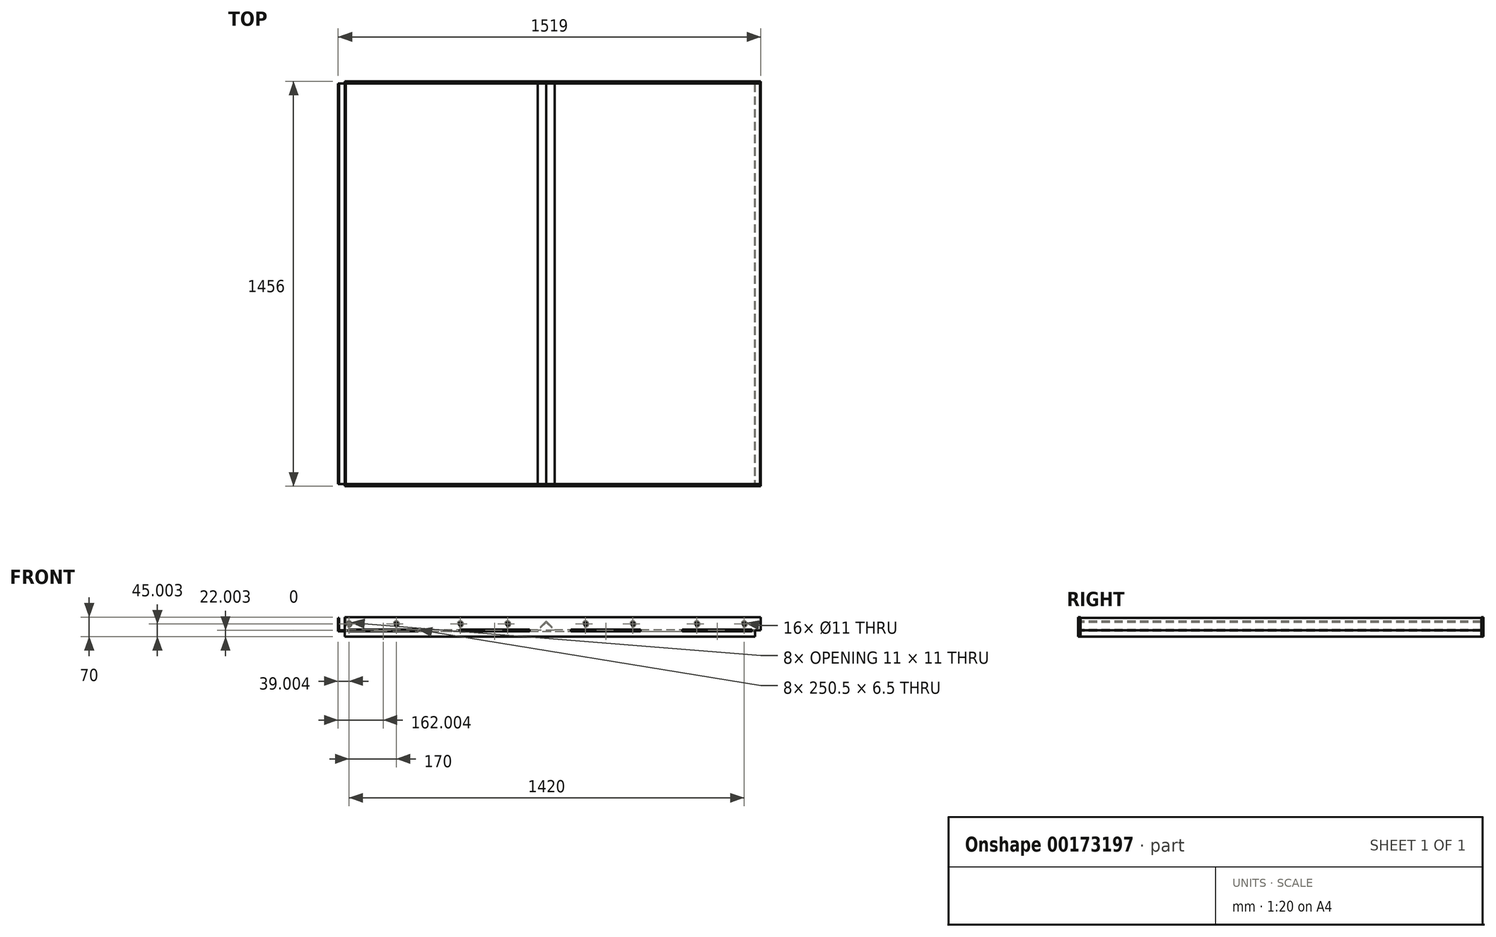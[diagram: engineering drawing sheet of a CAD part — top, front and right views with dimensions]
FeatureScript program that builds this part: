
annotation { "Feature Type Name" : "Feature", "Feature Type Description" : "" }
export const myFeature = defineFeature(function(context is Context, id is Id, definition is map)
    precondition{}
    {
        {
            var Q0;
            Q0=qCreatedBy(makeId("Front.planeOp"),FACE);
            var sketch = newSketch(context, id + "F0", { "sketchPlane" : qUnion([Q0])});
            skLineSegment(sketch, "E0", {"start": v(-1403.49, 88.26) * mm, "end": v(-1403.49, 40.26) * mm});
            skLineSegment(sketch, "E1", {"start": v(-1403.49, 40.26) * mm, "end": v(91.51, 40.26) * mm});
            skLineSegment(sketch, "E2", {"start": v(91.51, 40.26) * mm, "end": v(91.51, 21.26) * mm});
            skLineSegment(sketch, "E3", {"start": v(91.51, 21.26) * mm, "end": v(94.51, 21.26) * mm});
            skLineSegment(sketch, "E4", {"start": v(94.51, 21.26) * mm, "end": v(94.51, 43.26) * mm});
            skLineSegment(sketch, "E5", {"start": v(94.51, 43.26) * mm, "end": v(-627.23, 43.26) * mm});
            skLineSegment(sketch, "E6", {"start": v(-1400.49, 43.26) * mm, "end": v(-1400.49, 88.26) * mm});
            skLineSegment(sketch, "E7", {"start": v(-1400.49, 88.26) * mm, "end": v(-1403.49, 88.26) * mm});
            skLineSegment(sketch, "E8", {"start": v(-1379.49, 43.26) * mm, "end": v(-1379.49, 88.26) * mm});
            skLineSegment(sketch, "E9", {"start": v(-1379.49, 88.26) * mm, "end": v(-1376.49, 88.26) * mm});
            skLineSegment(sketch, "E10", {"start": v(-1376.49, 88.26) * mm, "end": v(-1376.49, 46.26) * mm});
            skLineSegment(sketch, "E11", {"start": v(-1376.49, 46.26) * mm, "end": v(-685.99, 46.26) * mm});
            skLineSegment(sketch, "E12", {"start": v(115.51, 46.26) * mm, "end": v(115.51, 43.26) * mm});
            skLineSegment(sketch, "E13", {"start": v(-1379.49, 43.26) * mm, "end": v(115.51, 43.26) * mm});
            skLineSegment(sketch, "E14", {"start": v(115.51, 46.26) * mm, "end": v(115.51, 88.26) * mm});
            skLineSegment(sketch, "E15", {"start": v(115.51, 88.26) * mm, "end": v(112.51, 88.26) * mm});
            skLineSegment(sketch, "E16", {"start": v(112.51, 88.26) * mm, "end": v(112.51, 46.26) * mm});
            skLineSegment(sketch, "E17.bottom", {"start": v(-1397.49, 82.67) * mm, "end": v(-1382.49, 82.67) * mm, "construction": true});
            skLineSegment(sketch, "E17.top", {"start": v(-1397.49, 47.75) * mm, "end": v(-1382.49, 47.75) * mm, "construction": true});
            skLineSegment(sketch, "E17.left", {"start": v(-1397.49, 82.67) * mm, "end": v(-1397.49, 47.75) * mm, "construction": true});
            skLineSegment(sketch, "E17.right", {"start": v(-1382.49, 82.67) * mm, "end": v(-1382.49, 47.75) * mm, "construction": true});
            skLineSegment(sketch, "E18", {"start": v(-655.99, 46.26) * mm, "end": v(-655.99, 76.26) * mm, "construction": true});
            skPoint(sketch, "E18.startSnap0", {"position": v(-655.99, 40.26) * mm});
            skLineSegment(sketch, "E19", {"start": v(-655.99, 76.26) * mm, "end": v(-685.99, 46.26) * mm});
            skLineSegment(sketch, "E20", {"start": v(-655.99, 76.26) * mm, "end": v(-625.99, 46.26) * mm});
            skPoint(sketch, "E21.orphan", {"position": v(-668.17, 64.08) * mm});
            skPoint(sketch, "E22.orphan", {"position": v(-643.8, 64.08) * mm});
            skLineSegment(sketch, "E23.0", {"start": v(-655.99, 72.02) * mm, "end": v(-684.74, 43.26) * mm});
            skLineSegment(sketch, "E24.0", {"start": v(-655.99, 72.02) * mm, "end": v(-627.23, 43.26) * mm});
            skLineSegment(sketch, "E25.trimOffspring", {"start": v(-625.99, 46.26) * mm, "end": v(112.51, 46.26) * mm});
            skLineSegment(sketch, "E26.trimOffspring", {"start": v(-684.74, 43.26) * mm, "end": v(-1400.49, 43.26) * mm});
            skSolve(sketch);
        }
        {
            var Q0;
            Q0=makeQuery(id+"F0.imprint","IMPRINT",FACE,{"disambiguationData":[TD([[makeQuery(id+"F0.imprint","IMPRINT",EDGE,{"derivedFrom":sQuery(id+"F0.wireOp",EDGE,"E0")}),1.0]])]});
            extrude(context, id + "F1", {"entities" : qUnion([Q0]), "oppositeDirection" : true, "depth" : 1440 * mm});
        }
        {
            var Q0;
            {var subQ0=sQuery(id+"F0.wireOp",EDGE,"E8");Q0=makeQuery(id+"F0.imprint","IMPRINT",FACE,{"disambiguationData":[TD([[makeQuery(id+"F0.imprint","IMPRINT",EDGE,{"derivedFrom":subQ0}),-1.0]])]});}
            extrude(context, id + "F2", {"entities" : qUnion([Q0]), "oppositeDirection" : true, "depth" : 1440 * mm});
        }
        {
            var Q0;
            Q0=makeQuery(id+"F2.opExtrude","SWEPT_FACE",FACE,{"disambiguationData":[OSD([sQuery(id+"F0.wireOp",EDGE,"E11")])]});
            var sketch = newSketch(context, id + "F3", { "sketchPlane" : qUnion([Q0])});
            skLineSegment(sketch, "E27.bottom", {"start": v(-1366.49, 0) * mm, "end": v(-1116.49, 0) * mm});
            skLineSegment(sketch, "E27.top", {"start": v(-1366.49, -7) * mm, "end": v(-1116.49, -7) * mm});
            skLineSegment(sketch, "E27.left", {"start": v(-1366.49, 0) * mm, "end": v(-1366.49, -7) * mm});
            skLineSegment(sketch, "E27.right", {"start": v(-1116.49, 0) * mm, "end": v(-1116.49, -7) * mm});
            skLineSegment(sketch, "E28.1.0.0", {"start": v(-966.49, -7) * mm, "end": v(-716.49, -7) * mm});
            skLineSegment(sketch, "E28.1.0.1", {"start": v(-966.49, 0) * mm, "end": v(-716.49, 0) * mm});
            skLineSegment(sketch, "E28.1.0.2", {"start": v(-966.49, 0) * mm, "end": v(-966.49, -7) * mm});
            skLineSegment(sketch, "E28.1.0.3", {"start": v(-716.49, 0) * mm, "end": v(-716.49, -7) * mm});
            skLineSegment(sketch, "E28.2.0.0", {"start": v(-566.49, -7) * mm, "end": v(-316.49, -7) * mm});
            skLineSegment(sketch, "E28.2.0.1", {"start": v(-566.49, 0) * mm, "end": v(-316.49, 0) * mm});
            skLineSegment(sketch, "E28.2.0.2", {"start": v(-566.49, 0) * mm, "end": v(-566.49, -7) * mm});
            skLineSegment(sketch, "E28.2.0.3", {"start": v(-316.49, 0) * mm, "end": v(-316.49, -7) * mm});
            skLineSegment(sketch, "E28.3.0.0", {"start": v(-166.49, -7) * mm, "end": v(83.51, -7) * mm});
            skLineSegment(sketch, "E28.3.0.1", {"start": v(-166.49, 0) * mm, "end": v(83.51, 0) * mm});
            skLineSegment(sketch, "E28.3.0.2", {"start": v(-166.49, 0) * mm, "end": v(-166.49, -7) * mm});
            skLineSegment(sketch, "E28.3.0.3", {"start": v(83.51, 0) * mm, "end": v(83.51, -7) * mm});
            skLineSegment(sketch, "E28.direction1", {"start": v(-1366.49, -7) * mm, "end": v(-966.49, -7) * mm, "construction": true});
            skLineSegment(sketch, "E29", {"start": v(-1376.49, 720) * mm, "end": v(410.62, 720) * mm, "construction": true});
            skPoint(sketch, "E29.endSnap0", {"position": v(112.51, 720) * mm});
            skLineSegment(sketch, "E30.MirrorCS", {"start": v(-966.49, 1440) * mm, "end": v(-966.49, 1447) * mm});
            skLineSegment(sketch, "E31.MirrorCS", {"start": v(-1366.49, 1440) * mm, "end": v(-1366.49, 1447) * mm});
            skLineSegment(sketch, "E32.MirrorCS", {"start": v(-106.49, 1440) * mm, "end": v(-106.49, 1447) * mm});
            skLineSegment(sketch, "E33.MirrorCS", {"start": v(-316.49, 1440) * mm, "end": v(-316.49, 1447) * mm});
            skLineSegment(sketch, "E34.MirrorCS", {"start": v(-566.49, 1440) * mm, "end": v(-566.49, 1447) * mm});
            skLineSegment(sketch, "E35.MirrorCS", {"start": v(-716.49, 1440) * mm, "end": v(-716.49, 1447) * mm});
            skLineSegment(sketch, "E36.MirrorCS", {"start": v(-1116.49, 1440) * mm, "end": v(-1116.49, 1447) * mm});
            skLineSegment(sketch, "E37.MirrorCS", {"start": v(93.51, 1440) * mm, "end": v(93.51, 1447) * mm});
            skLineSegment(sketch, "E38.MirrorCS", {"start": v(83.51, 1440) * mm, "end": v(83.51, 1447) * mm});
            skLineSegment(sketch, "E39.MirrorCS", {"start": v(-166.49, 1440) * mm, "end": v(-166.49, 1447) * mm});
            skLineSegment(sketch, "E40.MirrorCS", {"start": v(-1366.49, 1447) * mm, "end": v(-1116.49, 1447) * mm});
            skLineSegment(sketch, "E41.MirrorCS", {"start": v(-1366.49, 1447) * mm, "end": v(-966.49, 1447) * mm, "construction": true});
            skLineSegment(sketch, "E42.MirrorCS", {"start": v(-106.49, 1447) * mm, "end": v(93.51, 1447) * mm});
            skLineSegment(sketch, "E43.MirrorCS", {"start": v(-166.49, 1447) * mm, "end": v(83.51, 1447) * mm});
            skLineSegment(sketch, "E44.MirrorCS", {"start": v(-566.49, 1440) * mm, "end": v(-316.49, 1440) * mm});
            skLineSegment(sketch, "E45.MirrorCS", {"start": v(-566.49, 1447) * mm, "end": v(-316.49, 1447) * mm});
            skLineSegment(sketch, "E46.MirrorCS", {"start": v(-966.49, 1440) * mm, "end": v(-716.49, 1440) * mm});
            skLineSegment(sketch, "E47.MirrorCS", {"start": v(-966.49, 1447) * mm, "end": v(-716.49, 1447) * mm});
            skLineSegment(sketch, "E48.MirrorCS", {"start": v(-1366.49, 1440) * mm, "end": v(-1116.49, 1440) * mm});
            skLineSegment(sketch, "E49.MirrorCS", {"start": v(-106.49, 1440) * mm, "end": v(93.51, 1440) * mm});
            skLineSegment(sketch, "E50.MirrorCS", {"start": v(-166.49, 1440) * mm, "end": v(83.51, 1440) * mm});
            skSolve(sketch);
        }
        {
            var Q0;
            Q0=qSketchRegion(id+"F3",true);
            extrude(context, id + "F4", {"entities" : qUnion([Q0]), "operationType" : NewBodyOperationType.ADD, "oppositeDirection" : true, "depth" : 3 * mm});
        }
        {
            var Q0;
            {var subQ20=sQuery(id+"F0.wireOp",EDGE,"E1");var subQ29=sQuery(id+"F0.wireOp",EDGE,"E6");var subQ34=sQuery(id+"F0.wireOp",EDGE,"E0");var subQ35=sQuery(id+"F0.wireOp",EDGE,"E7");var subQ40=sQuery(id+"F0.wireOp",EDGE,"E13");var subQ41=sQuery(id+"F0.wireOp",EDGE,"E5");Q0=makeQuery(id+"FYbyz10K0Vfltxj_1.boolean.opBoolean","SPLIT",FACE,{"disambiguationData":[TD([makeQuery(id+"F1.opExtrude","SWEPT_FACE",FACE,{"disambiguationData":[OSD([subQ34])]})])],"derivedFrom":makeQuery(id+"F1.opExtrude","CAP_FACE",FACE,{"disambiguationData":[OSD([subQ34,subQ20,sQuery(id+"F0.wireOp",EDGE,"E2"),sQuery(id+"F0.wireOp",EDGE,"E3"),sQuery(id+"F0.wireOp",EDGE,"E4"),subQ41,subQ29,subQ35,subQ40])],"isStart":true})});}
            var sketch = newSketch(context, id + "F5", { "sketchPlane" : qUnion([Q0])});
            skLineSegment(sketch, "E51", {"start": v(115.51, 43.26) * mm, "end": v(94.51, 43.26) * mm});
            skLineSegment(sketch, "E52", {"start": v(94.51, 43.26) * mm, "end": v(94.51, 21.26) * mm});
            skLineSegment(sketch, "E53", {"start": v(94.51, 21.26) * mm, "end": v(-1379.49, 21.26) * mm});
            skLineSegment(sketch, "E54", {"start": v(-1379.49, 21.26) * mm, "end": v(-1379.49, 91.26) * mm});
            skLineSegment(sketch, "E55", {"start": v(-1379.49, 91.26) * mm, "end": v(115.51, 91.26) * mm});
            skLineSegment(sketch, "E56", {"start": v(115.51, 91.26) * mm, "end": v(115.51, 43.26) * mm});
            skLineSegment(sketch, "E57.bottom", {"start": v(-1366.74, 46.51) * mm, "end": v(-1116.24, 46.51) * mm});
            skLineSegment(sketch, "E57.top", {"start": v(-1366.74, 40.01) * mm, "end": v(-1116.24, 40.01) * mm});
            skLineSegment(sketch, "E57.left", {"start": v(-1366.74, 46.51) * mm, "end": v(-1366.74, 40.01) * mm});
            skLineSegment(sketch, "E57.right", {"start": v(-1116.24, 46.51) * mm, "end": v(-1116.24, 40.01) * mm});
            skLineSegment(sketch, "E58.1.0.0", {"start": v(-966.74, 46.51) * mm, "end": v(-716.24, 46.51) * mm});
            skLineSegment(sketch, "E58.1.0.1", {"start": v(-966.74, 40.01) * mm, "end": v(-716.24, 40.01) * mm});
            skLineSegment(sketch, "E58.1.0.2", {"start": v(-966.74, 46.51) * mm, "end": v(-966.74, 40.01) * mm});
            skLineSegment(sketch, "E58.1.0.3", {"start": v(-716.24, 46.51) * mm, "end": v(-716.24, 40.01) * mm});
            skLineSegment(sketch, "E58.2.0.0", {"start": v(-566.74, 46.51) * mm, "end": v(-316.24, 46.51) * mm});
            skLineSegment(sketch, "E58.2.0.1", {"start": v(-566.74, 40.01) * mm, "end": v(-316.24, 40.01) * mm});
            skLineSegment(sketch, "E58.2.0.2", {"start": v(-566.74, 46.51) * mm, "end": v(-566.74, 40.01) * mm});
            skLineSegment(sketch, "E58.2.0.3", {"start": v(-316.24, 46.51) * mm, "end": v(-316.24, 40.01) * mm});
            skLineSegment(sketch, "E58.3.0.0", {"start": v(-166.74, 46.51) * mm, "end": v(83.76, 46.51) * mm});
            skLineSegment(sketch, "E58.3.0.1", {"start": v(-166.74, 40.01) * mm, "end": v(83.76, 40.01) * mm});
            skLineSegment(sketch, "E58.3.0.2", {"start": v(-166.74, 46.51) * mm, "end": v(-166.74, 40.01) * mm});
            skLineSegment(sketch, "E58.3.0.3", {"start": v(83.76, 46.51) * mm, "end": v(83.76, 40.01) * mm});
            skLineSegment(sketch, "E58.direction1", {"start": v(-1366.74, 40.01) * mm, "end": v(-966.74, 40.01) * mm, "construction": true});
            skSolve(sketch);
        }
        {
            var Q0;
            Q0=qSketchRegion(id+"F5",true);
            extrude(context, id + "F6", {"entities" : qUnion([Q0]), "depth" : 8 * mm});
        }
        {
            var Q0;
            Q0=sQuery(id+"F3.wireOp",EDGE,"E29");
            cPlane(context, id + "F7", {"entities" : qUnion([Q0]), "cplaneType" : CPlaneType.LINE_ANGLE, "offset" : 25 * mm, "angle" : 0 * degree, "width" : 150 * mm, "height" : 150 * mm});
        }
        {
            var Q0;
            Q0=makeQuery(id+"F6.opExtrude","CAP_FACE",FACE,{"disambiguationData":[OSD([sQuery(id+"F5.wireOp",EDGE,"E51"),sQuery(id+"F5.wireOp",EDGE,"E52"),sQuery(id+"F5.wireOp",EDGE,"E53"),sQuery(id+"F5.wireOp",EDGE,"E54"),sQuery(id+"F5.wireOp",EDGE,"E55"),sQuery(id+"F5.wireOp",EDGE,"E56"),sQuery(id+"F5.wireOp",EDGE,"E57.bottom"),sQuery(id+"F5.wireOp",EDGE,"E57.top"),sQuery(id+"F5.wireOp",EDGE,"E57.left"),sQuery(id+"F5.wireOp",EDGE,"E57.right"),sQuery(id+"F5.wireOp",EDGE,"E58.1.0.0"),sQuery(id+"F5.wireOp",EDGE,"E58.1.0.1"),sQuery(id+"F5.wireOp",EDGE,"E58.1.0.2"),sQuery(id+"F5.wireOp",EDGE,"E58.1.0.3"),sQuery(id+"F5.wireOp",EDGE,"E58.2.0.0"),sQuery(id+"F5.wireOp",EDGE,"E58.2.0.1"),sQuery(id+"F5.wireOp",EDGE,"E58.2.0.2"),sQuery(id+"F5.wireOp",EDGE,"E58.2.0.3"),sQuery(id+"F5.wireOp",EDGE,"E58.3.0.0"),sQuery(id+"F5.wireOp",EDGE,"E58.3.0.1"),sQuery(id+"F5.wireOp",EDGE,"E58.3.0.2"),sQuery(id+"F5.wireOp",EDGE,"E58.3.0.3"),sQuery(id+"F5.wireOp",EDGE,"E58.4.0.0"),sQuery(id+"F5.wireOp",EDGE,"E58.4.0.1"),sQuery(id+"F5.wireOp",EDGE,"E58.4.0.2"),sQuery(id+"F5.wireOp",EDGE,"E58.4.0.3")])],"isStart":true});
            var sketch = newSketch(context, id + "F8", { "sketchPlane" : qUnion([Q0])});
            skPoint(sketch, "E59", {"position": v(-55.51, 66.26) * mm});
            skPoint(sketch, "E60", {"position": v(114.49, 66.26) * mm});
            skPoint(sketch, "E61", {"position": v(344.49, 66.26) * mm});
            skPoint(sketch, "E62", {"position": v(514.49, 66.26) * mm});
            skPoint(sketch, "E63", {"position": v(794.49, 66.26) * mm});
            skPoint(sketch, "E64", {"position": v(964.49, 66.26) * mm});
            skPoint(sketch, "E65", {"position": v(1194.49, 66.26) * mm});
            skPoint(sketch, "E66", {"position": v(1364.49, 66.26) * mm});
            skSolve(sketch);
        }
        {
            var Q0;
            Q0=sQuery(id+"F8.wireOp",VERTEX,"E66");
            var Q1;
            Q1=sQuery(id+"F8.wireOp",VERTEX,"E65");
            var Q2;
            Q2=sQuery(id+"F8.wireOp",VERTEX,"E64");
            var Q3;
            Q3=sQuery(id+"F8.wireOp",VERTEX,"E63");
            var Q4;
            Q4=sQuery(id+"F8.wireOp",VERTEX,"E62");
            var Q5;
            Q5=sQuery(id+"F8.wireOp",VERTEX,"E61");
            var Q6;
            Q6=sQuery(id+"F8.wireOp",VERTEX,"E60");
            var Q7;
            Q7=sQuery(id+"F8.wireOp",VERTEX,"E59");
            var Q8;
            Q8=makeQuery(id+"F6.opExtrude","SWEPT_BODY",BODY,{"disambiguationData":[OSD([sQuery(id+"F5.wireOp",EDGE,"E51"),sQuery(id+"F5.wireOp",EDGE,"E52"),sQuery(id+"F5.wireOp",EDGE,"E53"),sQuery(id+"F5.wireOp",EDGE,"E54"),sQuery(id+"F5.wireOp",EDGE,"E55"),sQuery(id+"F5.wireOp",EDGE,"E56"),sQuery(id+"F5.wireOp",EDGE,"E57.bottom"),sQuery(id+"F5.wireOp",EDGE,"E57.top"),sQuery(id+"F5.wireOp",EDGE,"E57.left"),sQuery(id+"F5.wireOp",EDGE,"E57.right"),sQuery(id+"F5.wireOp",EDGE,"E58.1.0.0"),sQuery(id+"F5.wireOp",EDGE,"E58.1.0.1"),sQuery(id+"F5.wireOp",EDGE,"E58.1.0.2"),sQuery(id+"F5.wireOp",EDGE,"E58.1.0.3"),sQuery(id+"F5.wireOp",EDGE,"E58.2.0.0"),sQuery(id+"F5.wireOp",EDGE,"E58.2.0.1"),sQuery(id+"F5.wireOp",EDGE,"E58.2.0.2"),sQuery(id+"F5.wireOp",EDGE,"E58.2.0.3"),sQuery(id+"F5.wireOp",EDGE,"E58.3.0.0"),sQuery(id+"F5.wireOp",EDGE,"E58.3.0.1"),sQuery(id+"F5.wireOp",EDGE,"E58.3.0.2"),sQuery(id+"F5.wireOp",EDGE,"E58.3.0.3"),sQuery(id+"F5.wireOp",EDGE,"E58.4.0.0"),sQuery(id+"F5.wireOp",EDGE,"E58.4.0.1"),sQuery(id+"F5.wireOp",EDGE,"E58.4.0.2"),sQuery(id+"F5.wireOp",EDGE,"E58.4.0.3")])]});
            hole(context, id + "F9", {"style" : HoleStyle.C_SINK, "endStyle" : HoleEndStyle.THROUGH, "holeDiameter" : 11 * mm, "cSinkDiameter" : 22 * mm, "cSinkAngle" : 90 * degree, "locations" : qUnion([Q0, Q1, Q2, Q3, Q4, Q5, Q6, Q7]), "scope" : qUnion([Q8]), "isTappedThrough" : true});
        }
        {
            var Q0;
            Q0=makeQuery(id+"F6.opExtrude","SWEPT_BODY",BODY,{"disambiguationData":[OSD([sQuery(id+"F5.wireOp",EDGE,"E51"),sQuery(id+"F5.wireOp",EDGE,"E52"),sQuery(id+"F5.wireOp",EDGE,"E53"),sQuery(id+"F5.wireOp",EDGE,"E54"),sQuery(id+"F5.wireOp",EDGE,"E55"),sQuery(id+"F5.wireOp",EDGE,"E56"),sQuery(id+"F5.wireOp",EDGE,"E57.bottom"),sQuery(id+"F5.wireOp",EDGE,"E57.top"),sQuery(id+"F5.wireOp",EDGE,"E57.left"),sQuery(id+"F5.wireOp",EDGE,"E57.right"),sQuery(id+"F5.wireOp",EDGE,"E58.1.0.0"),sQuery(id+"F5.wireOp",EDGE,"E58.1.0.1"),sQuery(id+"F5.wireOp",EDGE,"E58.1.0.2"),sQuery(id+"F5.wireOp",EDGE,"E58.1.0.3"),sQuery(id+"F5.wireOp",EDGE,"E58.2.0.0"),sQuery(id+"F5.wireOp",EDGE,"E58.2.0.1"),sQuery(id+"F5.wireOp",EDGE,"E58.2.0.2"),sQuery(id+"F5.wireOp",EDGE,"E58.2.0.3"),sQuery(id+"F5.wireOp",EDGE,"E58.3.0.0"),sQuery(id+"F5.wireOp",EDGE,"E58.3.0.1"),sQuery(id+"F5.wireOp",EDGE,"E58.3.0.2"),sQuery(id+"F5.wireOp",EDGE,"E58.3.0.3"),sQuery(id+"F5.wireOp",EDGE,"E58.4.0.0"),sQuery(id+"F5.wireOp",EDGE,"E58.4.0.1"),sQuery(id+"F5.wireOp",EDGE,"E58.4.0.2"),sQuery(id+"F5.wireOp",EDGE,"E58.4.0.3")])]});
            var Q1;
            Q1=qCreatedBy(id+"F7.planeOp",FACE);
            mirror(context, id + "F10", {"entities" : qUnion([Q0]), "mirrorPlane" : qUnion([Q1])});
        }
        {
            var Q0;
            Q0=makeQuery(id+"F2.opExtrude","SWEPT_FACE",FACE,{"disambiguationData":[OSD([sQuery(id+"F0.wireOp",EDGE,"E12"),sQuery(id+"F0.wireOp",EDGE,"E14")])]});
            cPlane(context, id + "F11", {"entities" : qUnion([Q0]), "cplaneType" : CPlaneType.OFFSET, "offset" : 25 * mm, "width" : 150 * mm, "height" : 150 * mm});
        }
    });
